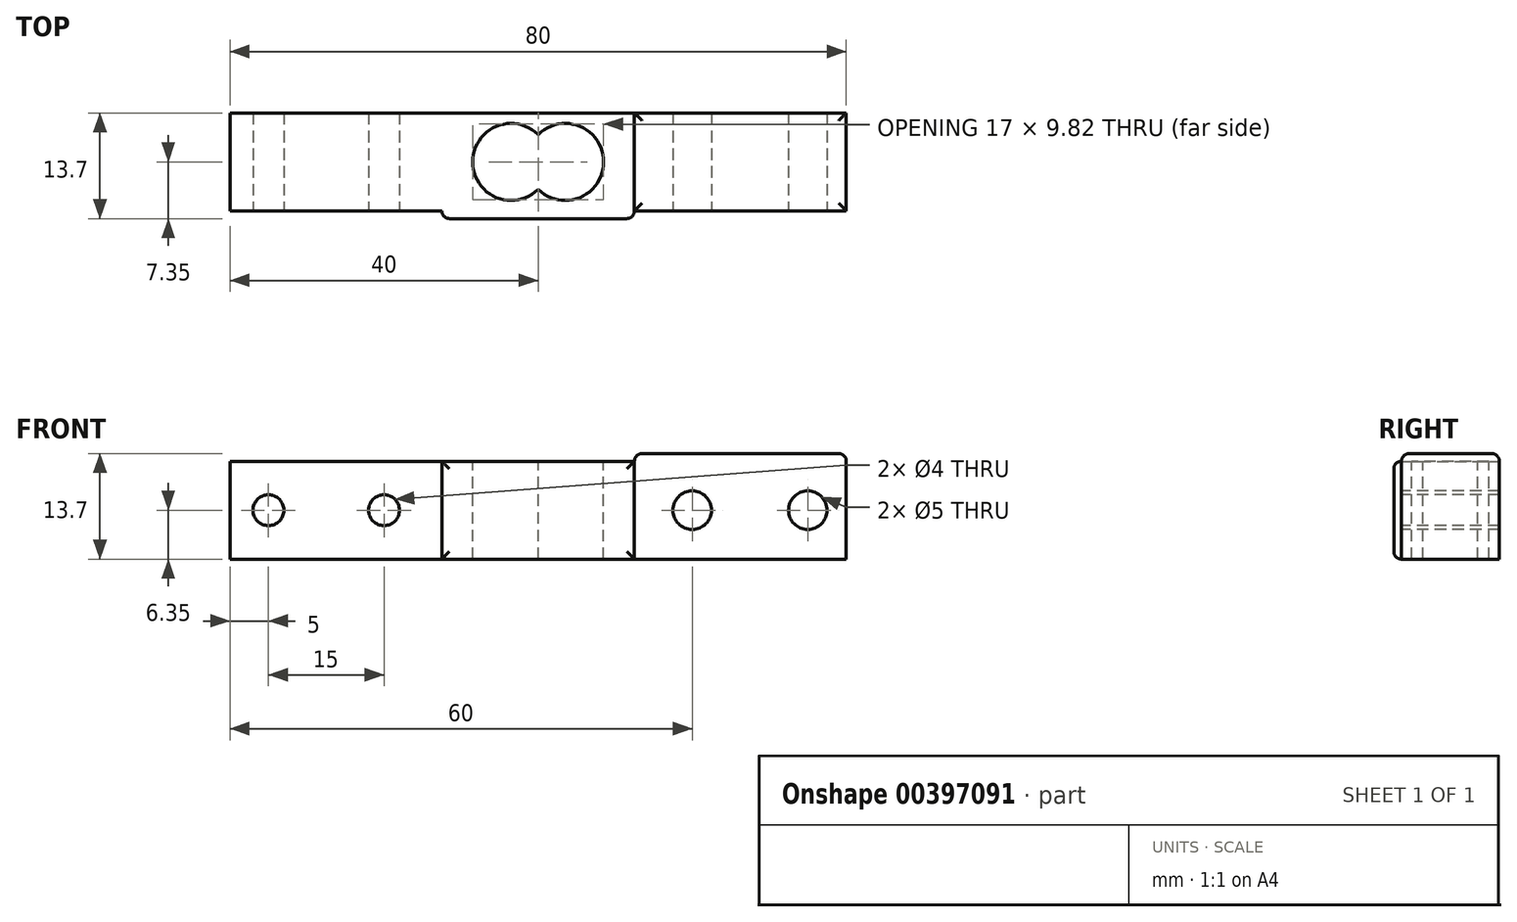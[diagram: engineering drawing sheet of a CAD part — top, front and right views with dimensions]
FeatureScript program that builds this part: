
annotation { "Feature Type Name" : "Feature", "Feature Type Description" : "" }
export const myFeature = defineFeature(function(context is Context, id is Id, definition is map)
    precondition{}
    {
        {
            var Q0;
            Q0=qCreatedBy(makeId("Front.planeOp"),FACE);
            var sketch = newSketch(context, id + "F0", { "sketchPlane" : qUnion([Q0])});
            skLineSegment(sketch, "E0.bottom", {"start": v(-40, -6.35) * mm, "end": v(40, -6.35) * mm});
            skLineSegment(sketch, "E0.top", {"start": v(-40, 6.35) * mm, "end": v(40, 6.35) * mm});
            skLineSegment(sketch, "E0.left", {"start": v(-40, -6.35) * mm, "end": v(-40, 6.35) * mm});
            skLineSegment(sketch, "E0.right", {"start": v(40, -6.35) * mm, "end": v(40, 6.35) * mm});
            skPoint(sketch, "E0.middle", {"position": v(0, 0) * mm});
            skSolve(sketch);
        }
        {
            var Q0;
            Q0=qSketchRegion(id+"F0",true);
            extrude(context, id + "F1", {"entities" : qUnion([Q0]), "endBound" : BoundingType.SYMMETRIC, "depth" : 12.7 * mm});
        }
        {
            var Q0;
            Q0=makeQuery(id+"F1.opExtrude","CAP_FACE",FACE,{"disambiguationData":[OSD([sQuery(id+"F0.wireOp",EDGE,"E0.bottom"),sQuery(id+"F0.wireOp",EDGE,"E0.top"),sQuery(id+"F0.wireOp",EDGE,"E0.left"),sQuery(id+"F0.wireOp",EDGE,"E0.right")])],"isStart":false});
            var sketch = newSketch(context, id + "F2", { "sketchPlane" : qUnion([Q0])});
            skCircle(sketch, "E1", {"center": v(-35, 0) * mm, "radius": 2 * mm});
            skCircle(sketch, "E2.1.0.0", {"center": v(-20, 0) * mm, "radius": 2 * mm});
            skLineSegment(sketch, "E2.direction1", {"start": v(-35, 0) * mm, "end": v(-20, 0) * mm, "construction": true});
            skCircle(sketch, "E3", {"center": v(35, 0) * mm, "radius": 2.5 * mm});
            skCircle(sketch, "E4.1.0.0", {"center": v(20, 0) * mm, "radius": 2.5 * mm});
            skLineSegment(sketch, "E4.direction1", {"start": v(35, 0) * mm, "end": v(20, 0) * mm, "construction": true});
            skSolve(sketch);
        }
        {
            var Q0;
            Q0=qSketchRegion(id+"F2",true);
            extrude(context, id + "F3", {"entities" : qUnion([Q0]), "operationType" : NewBodyOperationType.REMOVE, "endBound" : BoundingType.THROUGH_ALL, "oppositeDirection" : true, "depth" : 25 * mm});
        }
        {
            var Q0;
            Q0=makeQuery(id+"F1.opExtrude","SWEPT_FACE",FACE,{"disambiguationData":[OSD([sQuery(id+"F0.wireOp",EDGE,"E0.top")])]});
            var sketch = newSketch(context, id + "F4", { "sketchPlane" : qUnion([Q0])});
            skCircle(sketch, "E5", {"center": v(3.5, 0) * mm, "radius": 5 * mm});
            skCircle(sketch, "E6", {"center": v(-3.5, 0) * mm, "radius": 5 * mm});
            skSolve(sketch);
        }
        {
            var Q0;
            Q0=qSketchRegion(id+"F4",true);
            extrude(context, id + "F5", {"entities" : qUnion([Q0]), "operationType" : NewBodyOperationType.REMOVE, "endBound" : BoundingType.THROUGH_ALL, "oppositeDirection" : true, "depth" : 25 * mm});
        }
        {
            var Q0;
            Q0=makeQuery(id+"F1.opExtrude","CAP_FACE",FACE,{"disambiguationData":[OSD([sQuery(id+"F0.wireOp",EDGE,"E0.bottom"),sQuery(id+"F0.wireOp",EDGE,"E0.top"),sQuery(id+"F0.wireOp",EDGE,"E0.left"),sQuery(id+"F0.wireOp",EDGE,"E0.right")])],"isStart":false});
            var sketch = newSketch(context, id + "F6", { "sketchPlane" : qUnion([Q0])});
            skLineSegment(sketch, "E7.bottom", {"start": v(12.5, -6.35) * mm, "end": v(-12.5, -6.35) * mm});
            skLineSegment(sketch, "E7.top", {"start": v(12.5, 6.35) * mm, "end": v(-12.5, 6.35) * mm});
            skLineSegment(sketch, "E7.left", {"start": v(12.5, -6.35) * mm, "end": v(12.5, 6.35) * mm});
            skLineSegment(sketch, "E7.right", {"start": v(-12.5, -6.35) * mm, "end": v(-12.5, 6.35) * mm});
            skPoint(sketch, "E7.middle", {"position": v(0, 0) * mm});
            skSolve(sketch);
        }
        {
            var Q0;
            Q0=qSketchRegion(id+"F6",true);
            extrude(context, id + "F7", {"entities" : qUnion([Q0]), "operationType" : NewBodyOperationType.ADD, "depth" : 1 * mm});
        }
        {
            var Q0;
            Q0=makeQuery(id+"F7.boolean.opBoolean","MERGE",FACE,{"derivedFrom":[makeQuery(id+"F1.opExtrude","SWEPT_FACE",FACE,{"disambiguationData":[OSD([sQuery(id+"F0.wireOp",EDGE,"E0.top")])]}),makeQuery(id+"F7.opExtrude","SWEPT_FACE",FACE,{"disambiguationData":[OSD([sQuery(id+"F6.wireOp",EDGE,"E7.top")])]})]});
            var sketch = newSketch(context, id + "F8", { "sketchPlane" : qUnion([Q0])});
            skLineSegment(sketch, "E8.bottom", {"start": v(40, 6.35) * mm, "end": v(12.5, 6.35) * mm});
            skLineSegment(sketch, "E8.top", {"start": v(40, -6.35) * mm, "end": v(12.5, -6.35) * mm});
            skLineSegment(sketch, "E8.left", {"start": v(40, 6.35) * mm, "end": v(40, -6.35) * mm});
            skLineSegment(sketch, "E8.right", {"start": v(12.5, 6.35) * mm, "end": v(12.5, -6.35) * mm});
            skSolve(sketch);
        }
        {
            var Q0;
            Q0=qSketchRegion(id+"F8",true);
            extrude(context, id + "F9", {"entities" : qUnion([Q0]), "operationType" : NewBodyOperationType.ADD, "depth" : 1 * mm});
        }
        {
            var Q0;
            Q0=makeQuery(id+"F9.opExtrude","CAP_EDGE",EDGE,{"disambiguationData":[OSD([sQuery(id+"F8.wireOp",EDGE,"E8.right")])],"isStart":false});
            var Q1;
            Q1=makeQuery(id+"F9.opExtrude","CAP_EDGE",EDGE,{"disambiguationData":[OSD([sQuery(id+"F8.wireOp",EDGE,"E8.left")])],"isStart":false});
            var Q2;
            Q2=makeQuery(id+"F7.opExtrude","CAP_EDGE",EDGE,{"disambiguationData":[OSD([sQuery(id+"F6.wireOp",EDGE,"E7.top")])],"isStart":false});
            var Q3;
            Q3=makeQuery(id+"F7.opExtrude","CAP_EDGE",EDGE,{"disambiguationData":[OSD([sQuery(id+"F6.wireOp",EDGE,"E7.bottom")])],"isStart":false});
            var Q4;
            Q4=makeQuery(id+"F7.opExtrude","CAP_FACE",FACE,{"disambiguationData":[OSD([sQuery(id+"F6.wireOp",EDGE,"E7.bottom"),sQuery(id+"F6.wireOp",EDGE,"E7.top"),sQuery(id+"F6.wireOp",EDGE,"E7.left"),sQuery(id+"F6.wireOp",EDGE,"E7.right")])],"isStart":false});
            var Q5;
            Q5=makeQuery(id+"F9.opExtrude","CAP_FACE",FACE,{"disambiguationData":[OSD([sQuery(id+"F8.wireOp",EDGE,"E8.bottom"),sQuery(id+"F8.wireOp",EDGE,"E8.top"),sQuery(id+"F8.wireOp",EDGE,"E8.left"),sQuery(id+"F8.wireOp",EDGE,"E8.right")])],"isStart":false});
            fillet(context, id + "F10", {"entities" : qUnion([Q0, Q1, Q2, Q3, Q4, Q5]), "radius" : 1 * mm, "tangentPropagation" : true, "allowEdgeOverflow" : false});
        }
    });
